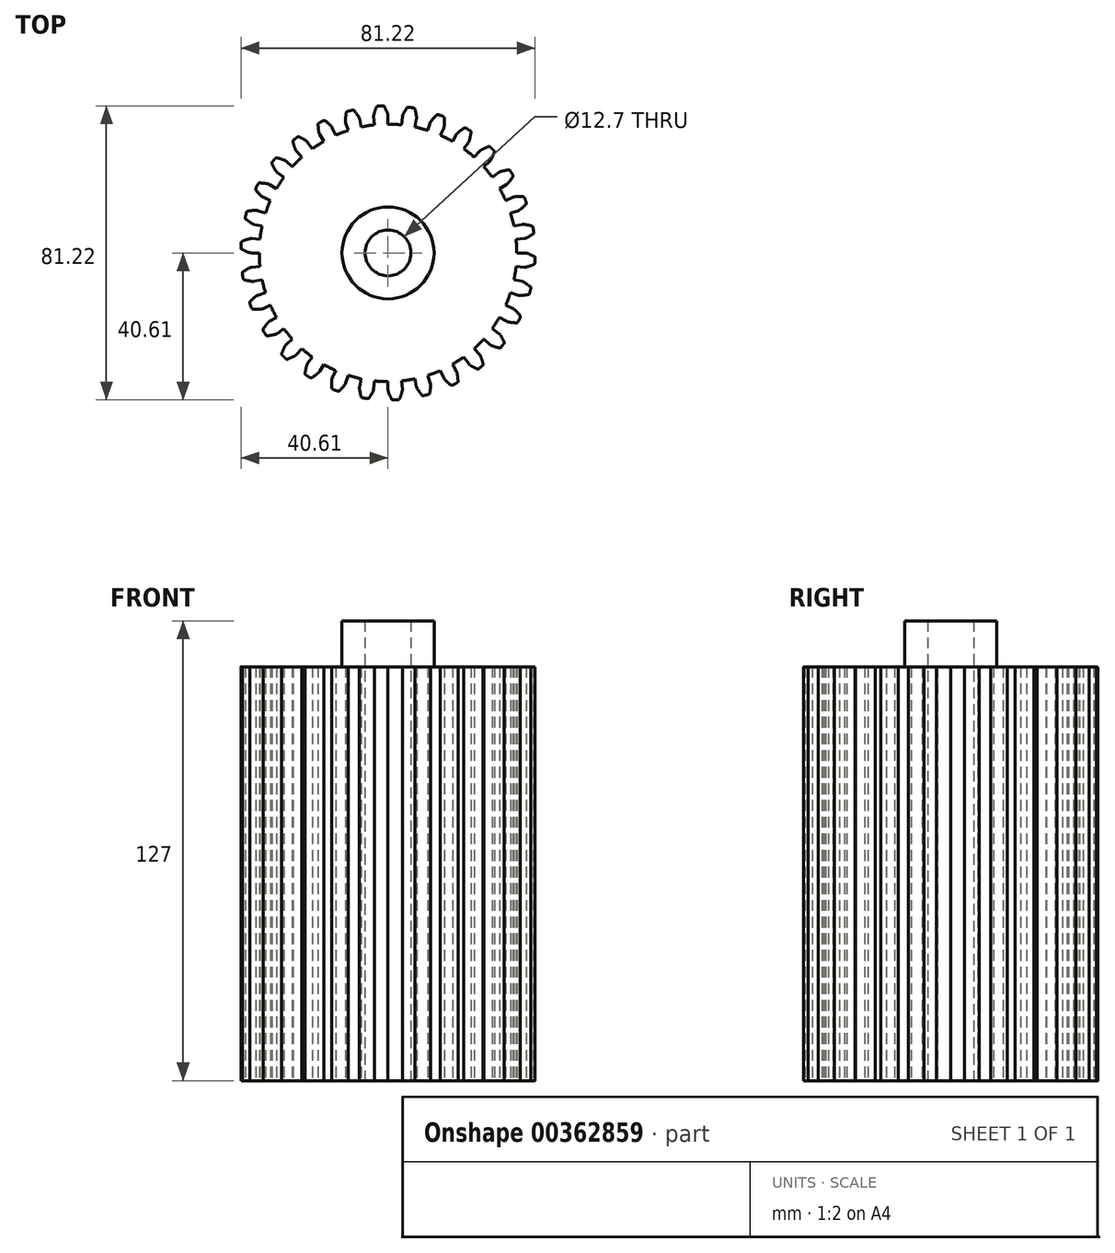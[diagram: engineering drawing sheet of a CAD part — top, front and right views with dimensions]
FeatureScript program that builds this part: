
annotation { "Feature Type Name" : "Feature", "Feature Type Description" : "" }
export const myFeature = defineFeature(function(context is Context, id is Id, definition is map)
    precondition{}
    {
        {
            var Q0;
            Q0=qCreatedBy(makeId("Top.planeOp"),FACE);
            var sketch = newSketch(context, id + "F0", { "sketchPlane" : qUnion([Q0])});
            skArc(sketch, "E0", {"start": v(-1.45, 40.61) * mm, "mid": v(-2.13, 40.58) * mm, "end": v(-2.8, 40.54) * mm});
            skArc(sketch, "E1", {"start": v(-3.72, 35.37) * mm, "mid": v(-5.56, 35.12) * mm, "end": v(-7.4, 34.78) * mm});
            skLineSegment(sketch, "E2", {"start": v(0, 37.81) * mm, "end": v(0, 35.56) * mm});
            skArc(sketch, "E3.trimOffspring", {"start": v(-0.1, 38.38) * mm, "mid": v(-0.51, 39.37) * mm, "end": v(-0.98, 40.34) * mm});
            skArc(sketch, "E4.MirrorCS", {"start": v(-3.9, 38.18) * mm, "mid": v(-3.6, 39.2) * mm, "end": v(-3.25, 40.22) * mm});
            skLineSegment(sketch, "E5.MirrorCS", {"start": v(-3.72, 35.37) * mm, "end": v(-3.95, 37.6) * mm});
            skPoint(sketch, "E6.visualSharp", {"position": v(-1.12, 40.62) * mm});
            skArc(sketch, "E6.filletArc", {"start": v(-0.98, 40.34) * mm, "mid": v(-1.17, 40.54) * mm, "end": v(-1.45, 40.61) * mm});
            skPoint(sketch, "E7.visualSharp", {"position": v(-3.13, 40.52) * mm});
            skArc(sketch, "E7.filletArc", {"start": v(-2.8, 40.54) * mm, "mid": v(-3.07, 40.44) * mm, "end": v(-3.25, 40.22) * mm});
            skPoint(sketch, "E8.visualSharp", {"position": v(0, 38.1) * mm});
            skArc(sketch, "E8.filletArc", {"start": v(0, 37.81) * mm, "mid": v(-0.03, 38.1) * mm, "end": v(-0.1, 38.38) * mm});
            skPoint(sketch, "E9.visualSharp", {"position": v(-3.98, 37.9) * mm});
            skArc(sketch, "E9.filletArc", {"start": v(-3.9, 38.18) * mm, "mid": v(-3.96, 37.9) * mm, "end": v(-3.95, 37.6) * mm});
            skLineSegment(sketch, "E10.1.0", {"start": v(-7.86, 36.99) * mm, "end": v(-7.4, 34.78) * mm});
            skArc(sketch, "E10.1.1", {"start": v(-7.86, 36.99) * mm, "mid": v(-7.95, 37.26) * mm, "end": v(-8.08, 37.52) * mm});
            skArc(sketch, "E10.1.2", {"start": v(-8.08, 37.52) * mm, "mid": v(-8.69, 38.4) * mm, "end": v(-9.34, 39.25) * mm});
            skArc(sketch, "E10.1.3", {"start": v(-9.34, 39.25) * mm, "mid": v(-9.57, 39.42) * mm, "end": v(-9.86, 39.43) * mm});
            skArc(sketch, "E10.1.4", {"start": v(-9.86, 39.43) * mm, "mid": v(-10.52, 39.26) * mm, "end": v(-11.18, 39.07) * mm});
            skArc(sketch, "E10.1.5", {"start": v(-11.18, 39.07) * mm, "mid": v(-11.42, 38.92) * mm, "end": v(-11.54, 38.66) * mm});
            skArc(sketch, "E10.1.6", {"start": v(-11.76, 36.53) * mm, "mid": v(-11.68, 37.6) * mm, "end": v(-11.54, 38.66) * mm});
            skArc(sketch, "E10.1.7", {"start": v(-11.76, 36.53) * mm, "mid": v(-11.75, 36.24) * mm, "end": v(-11.69, 35.96) * mm});
            skLineSegment(sketch, "E10.1.8", {"start": v(-10.99, 33.82) * mm, "end": v(-11.69, 35.96) * mm});
            skLineSegment(sketch, "E10.2.0", {"start": v(-15.38, 34.54) * mm, "end": v(-14.46, 32.49) * mm});
            skArc(sketch, "E10.2.1", {"start": v(-15.38, 34.54) * mm, "mid": v(-15.52, 34.8) * mm, "end": v(-15.7, 35.02) * mm});
            skArc(sketch, "E10.2.2", {"start": v(-15.7, 35.02) * mm, "mid": v(-16.48, 35.76) * mm, "end": v(-17.3, 36.45) * mm});
            skArc(sketch, "E10.2.3", {"start": v(-17.3, 36.45) * mm, "mid": v(-17.56, 36.56) * mm, "end": v(-17.84, 36.52) * mm});
            skArc(sketch, "E10.2.4", {"start": v(-17.84, 36.52) * mm, "mid": v(-18.45, 36.21) * mm, "end": v(-19.06, 35.9) * mm});
            skArc(sketch, "E10.2.5", {"start": v(-19.06, 35.9) * mm, "mid": v(-19.26, 35.7) * mm, "end": v(-19.32, 35.42) * mm});
            skArc(sketch, "E10.2.6", {"start": v(-19.1, 33.29) * mm, "mid": v(-19.24, 34.35) * mm, "end": v(-19.32, 35.42) * mm});
            skArc(sketch, "E10.2.7", {"start": v(-19.1, 33.29) * mm, "mid": v(-19.03, 33) * mm, "end": v(-18.9, 32.75) * mm});
            skLineSegment(sketch, "E10.2.8", {"start": v(-17.78, 30.8) * mm, "end": v(-18.9, 32.75) * mm});
            skLineSegment(sketch, "E10.3.0", {"start": v(-22.23, 30.6) * mm, "end": v(-20.9, 28.77) * mm});
            skArc(sketch, "E10.3.1", {"start": v(-22.23, 30.6) * mm, "mid": v(-22.42, 30.8) * mm, "end": v(-22.64, 30.99) * mm});
            skArc(sketch, "E10.3.2", {"start": v(-22.64, 30.99) * mm, "mid": v(-23.56, 31.55) * mm, "end": v(-24.5, 32.06) * mm});
            skArc(sketch, "E10.3.3", {"start": v(-24.5, 32.06) * mm, "mid": v(-24.78, 32.11) * mm, "end": v(-25.04, 32) * mm});
            skArc(sketch, "E10.3.4", {"start": v(-25.04, 32) * mm, "mid": v(-25.58, 31.58) * mm, "end": v(-26.1, 31.15) * mm});
            skArc(sketch, "E10.3.5", {"start": v(-26.1, 31.15) * mm, "mid": v(-26.26, 30.91) * mm, "end": v(-26.27, 30.63) * mm});
            skArc(sketch, "E10.3.6", {"start": v(-25.6, 28.6) * mm, "mid": v(-25.96, 29.6) * mm, "end": v(-26.27, 30.63) * mm});
            skArc(sketch, "E10.3.7", {"start": v(-25.6, 28.6) * mm, "mid": v(-25.48, 28.33) * mm, "end": v(-25.3, 28.1) * mm});
            skLineSegment(sketch, "E10.3.8", {"start": v(-23.8, 26.43) * mm, "end": v(-25.3, 28.1) * mm});
            skLineSegment(sketch, "E10.4.0", {"start": v(-28.1, 25.3) * mm, "end": v(-26.43, 23.8) * mm});
            skArc(sketch, "E10.4.1", {"start": v(-28.1, 25.3) * mm, "mid": v(-28.33, 25.48) * mm, "end": v(-28.6, 25.6) * mm});
            skArc(sketch, "E10.4.2", {"start": v(-28.6, 25.6) * mm, "mid": v(-29.6, 25.96) * mm, "end": v(-30.63, 26.27) * mm});
            skArc(sketch, "E10.4.3", {"start": v(-30.63, 26.27) * mm, "mid": v(-30.91, 26.26) * mm, "end": v(-31.15, 26.1) * mm});
            skArc(sketch, "E10.4.4", {"start": v(-31.15, 26.1) * mm, "mid": v(-31.58, 25.58) * mm, "end": v(-32, 25.04) * mm});
            skArc(sketch, "E10.4.5", {"start": v(-32, 25.04) * mm, "mid": v(-32.11, 24.78) * mm, "end": v(-32.06, 24.5) * mm});
            skArc(sketch, "E10.4.6", {"start": v(-30.99, 22.64) * mm, "mid": v(-31.55, 23.56) * mm, "end": v(-32.06, 24.5) * mm});
            skArc(sketch, "E10.4.7", {"start": v(-30.99, 22.64) * mm, "mid": v(-30.8, 22.42) * mm, "end": v(-30.6, 22.23) * mm});
            skLineSegment(sketch, "E10.4.8", {"start": v(-28.77, 20.9) * mm, "end": v(-30.6, 22.23) * mm});
            skLineSegment(sketch, "E10.5.0", {"start": v(-32.75, 18.9) * mm, "end": v(-30.8, 17.78) * mm});
            skArc(sketch, "E10.5.1", {"start": v(-32.75, 18.9) * mm, "mid": v(-33, 19.03) * mm, "end": v(-33.29, 19.1) * mm});
            skArc(sketch, "E10.5.2", {"start": v(-33.29, 19.1) * mm, "mid": v(-34.35, 19.24) * mm, "end": v(-35.42, 19.32) * mm});
            skArc(sketch, "E10.5.3", {"start": v(-35.42, 19.32) * mm, "mid": v(-35.7, 19.26) * mm, "end": v(-35.9, 19.06) * mm});
            skArc(sketch, "E10.5.4", {"start": v(-35.9, 19.06) * mm, "mid": v(-36.21, 18.45) * mm, "end": v(-36.52, 17.84) * mm});
            skArc(sketch, "E10.5.5", {"start": v(-36.52, 17.84) * mm, "mid": v(-36.56, 17.56) * mm, "end": v(-36.45, 17.3) * mm});
            skArc(sketch, "E10.5.6", {"start": v(-35.02, 15.7) * mm, "mid": v(-35.76, 16.48) * mm, "end": v(-36.45, 17.3) * mm});
            skArc(sketch, "E10.5.7", {"start": v(-35.02, 15.7) * mm, "mid": v(-34.8, 15.52) * mm, "end": v(-34.54, 15.38) * mm});
            skLineSegment(sketch, "E10.5.8", {"start": v(-32.49, 14.46) * mm, "end": v(-34.54, 15.38) * mm});
            skLineSegment(sketch, "E10.6.0", {"start": v(-35.96, 11.69) * mm, "end": v(-33.82, 10.99) * mm});
            skArc(sketch, "E10.6.1", {"start": v(-35.96, 11.69) * mm, "mid": v(-36.24, 11.75) * mm, "end": v(-36.53, 11.76) * mm});
            skArc(sketch, "E10.6.2", {"start": v(-36.53, 11.76) * mm, "mid": v(-37.6, 11.68) * mm, "end": v(-38.66, 11.54) * mm});
            skArc(sketch, "E10.6.3", {"start": v(-38.66, 11.54) * mm, "mid": v(-38.92, 11.42) * mm, "end": v(-39.07, 11.18) * mm});
            skArc(sketch, "E10.6.4", {"start": v(-39.07, 11.18) * mm, "mid": v(-39.26, 10.52) * mm, "end": v(-39.43, 9.86) * mm});
            skArc(sketch, "E10.6.5", {"start": v(-39.43, 9.86) * mm, "mid": v(-39.42, 9.57) * mm, "end": v(-39.25, 9.34) * mm});
            skArc(sketch, "E10.6.6", {"start": v(-37.52, 8.08) * mm, "mid": v(-38.4, 8.69) * mm, "end": v(-39.25, 9.34) * mm});
            skArc(sketch, "E10.6.7", {"start": v(-37.52, 8.08) * mm, "mid": v(-37.26, 7.95) * mm, "end": v(-36.99, 7.86) * mm});
            skLineSegment(sketch, "E10.6.8", {"start": v(-34.78, 7.4) * mm, "end": v(-36.99, 7.86) * mm});
            skLineSegment(sketch, "E10.7.0", {"start": v(-37.6, 3.95) * mm, "end": v(-35.37, 3.72) * mm});
            skArc(sketch, "E10.7.1", {"start": v(-37.6, 3.95) * mm, "mid": v(-37.9, 3.96) * mm, "end": v(-38.18, 3.9) * mm});
            skArc(sketch, "E10.7.2", {"start": v(-38.18, 3.9) * mm, "mid": v(-39.2, 3.6) * mm, "end": v(-40.22, 3.25) * mm});
            skArc(sketch, "E10.7.3", {"start": v(-40.22, 3.25) * mm, "mid": v(-40.44, 3.07) * mm, "end": v(-40.54, 2.8) * mm});
            skArc(sketch, "E10.7.4", {"start": v(-40.54, 2.8) * mm, "mid": v(-40.58, 2.13) * mm, "end": v(-40.61, 1.45) * mm});
            skArc(sketch, "E10.7.5", {"start": v(-40.61, 1.45) * mm, "mid": v(-40.54, 1.17) * mm, "end": v(-40.34, 0.98) * mm});
            skArc(sketch, "E10.7.6", {"start": v(-38.38, 0.1) * mm, "mid": v(-39.37, 0.51) * mm, "end": v(-40.34, 0.98) * mm});
            skArc(sketch, "E10.7.7", {"start": v(-38.38, 0.1) * mm, "mid": v(-38.1, 0.03) * mm, "end": v(-37.81, 0) * mm});
            skLineSegment(sketch, "E10.7.8", {"start": v(-35.56, 0) * mm, "end": v(-37.81, 0) * mm});
            skLineSegment(sketch, "E10.8.0", {"start": v(-37.6, -3.95) * mm, "end": v(-35.37, -3.72) * mm});
            skArc(sketch, "E10.8.1", {"start": v(-37.6, -3.95) * mm, "mid": v(-37.9, -4) * mm, "end": v(-38.16, -4.12) * mm});
            skArc(sketch, "E10.8.2", {"start": v(-38.16, -4.12) * mm, "mid": v(-39.1, -4.63) * mm, "end": v(-40.02, -5.19) * mm});
            skArc(sketch, "E10.8.3", {"start": v(-40.02, -5.19) * mm, "mid": v(-40.2, -5.4) * mm, "end": v(-40.24, -5.68) * mm});
            skArc(sketch, "E10.8.4", {"start": v(-40.24, -5.68) * mm, "mid": v(-40.14, -6.36) * mm, "end": v(-40.03, -7.03) * mm});
            skArc(sketch, "E10.8.5", {"start": v(-40.03, -7.03) * mm, "mid": v(-39.9, -7.29) * mm, "end": v(-39.66, -7.43) * mm});
            skArc(sketch, "E10.8.6", {"start": v(-37.56, -7.88) * mm, "mid": v(-38.62, -7.68) * mm, "end": v(-39.66, -7.43) * mm});
            skArc(sketch, "E10.8.7", {"start": v(-37.56, -7.88) * mm, "mid": v(-37.27, -7.9) * mm, "end": v(-36.99, -7.86) * mm});
            skLineSegment(sketch, "E10.8.8", {"start": v(-34.78, -7.4) * mm, "end": v(-36.99, -7.86) * mm});
            skLineSegment(sketch, "E10.9.0", {"start": v(-35.96, -11.69) * mm, "end": v(-33.82, -10.99) * mm});
            skArc(sketch, "E10.9.1", {"start": v(-35.96, -11.69) * mm, "mid": v(-36.23, -11.8) * mm, "end": v(-36.47, -11.96) * mm});
            skArc(sketch, "E10.9.2", {"start": v(-36.47, -11.96) * mm, "mid": v(-37.29, -12.65) * mm, "end": v(-38.06, -13.4) * mm});
            skArc(sketch, "E10.9.3", {"start": v(-38.06, -13.4) * mm, "mid": v(-38.2, -13.64) * mm, "end": v(-38.18, -13.93) * mm});
            skArc(sketch, "E10.9.4", {"start": v(-38.18, -13.93) * mm, "mid": v(-37.94, -14.56) * mm, "end": v(-37.7, -15.2) * mm});
            skArc(sketch, "E10.9.5", {"start": v(-37.7, -15.2) * mm, "mid": v(-37.52, -15.42) * mm, "end": v(-37.25, -15.52) * mm});
            skArc(sketch, "E10.9.6", {"start": v(-35.1, -15.52) * mm, "mid": v(-36.18, -15.54) * mm, "end": v(-37.25, -15.52) * mm});
            skArc(sketch, "E10.9.7", {"start": v(-35.1, -15.52) * mm, "mid": v(-34.82, -15.47) * mm, "end": v(-34.54, -15.38) * mm});
            skLineSegment(sketch, "E10.9.8", {"start": v(-32.49, -14.46) * mm, "end": v(-34.54, -15.38) * mm});
            skLineSegment(sketch, "E10.10.0", {"start": v(-32.75, -18.9) * mm, "end": v(-30.8, -17.78) * mm});
            skArc(sketch, "E10.10.1", {"start": v(-32.75, -18.9) * mm, "mid": v(-32.98, -19.07) * mm, "end": v(-33.19, -19.28) * mm});
            skArc(sketch, "E10.10.2", {"start": v(-33.19, -19.28) * mm, "mid": v(-33.84, -20.13) * mm, "end": v(-34.45, -21.01) * mm});
            skArc(sketch, "E10.10.3", {"start": v(-34.45, -21.01) * mm, "mid": v(-34.53, -21.29) * mm, "end": v(-34.45, -21.56) * mm});
            skArc(sketch, "E10.10.4", {"start": v(-34.45, -21.56) * mm, "mid": v(-34.08, -22.13) * mm, "end": v(-33.7, -22.7) * mm});
            skArc(sketch, "E10.10.5", {"start": v(-33.7, -22.7) * mm, "mid": v(-33.49, -22.88) * mm, "end": v(-33.2, -22.92) * mm});
            skArc(sketch, "E10.10.6", {"start": v(-31.11, -22.47) * mm, "mid": v(-32.15, -22.73) * mm, "end": v(-33.2, -22.92) * mm});
            skArc(sketch, "E10.10.7", {"start": v(-31.11, -22.47) * mm, "mid": v(-30.84, -22.37) * mm, "end": v(-30.6, -22.23) * mm});
            skLineSegment(sketch, "E10.10.8", {"start": v(-28.77, -20.9) * mm, "end": v(-30.6, -22.23) * mm});
            skLineSegment(sketch, "E10.11.0", {"start": v(-28.1, -25.3) * mm, "end": v(-26.43, -23.8) * mm});
            skArc(sketch, "E10.11.1", {"start": v(-28.1, -25.3) * mm, "mid": v(-28.3, -25.51) * mm, "end": v(-28.45, -25.76) * mm});
            skArc(sketch, "E10.11.2", {"start": v(-28.45, -25.76) * mm, "mid": v(-28.91, -26.73) * mm, "end": v(-29.32, -27.72) * mm});
            skArc(sketch, "E10.11.3", {"start": v(-29.32, -27.72) * mm, "mid": v(-29.35, -28) * mm, "end": v(-29.22, -28.25) * mm});
            skArc(sketch, "E10.11.4", {"start": v(-29.22, -28.25) * mm, "mid": v(-28.74, -28.74) * mm, "end": v(-28.25, -29.22) * mm});
            skArc(sketch, "E10.11.5", {"start": v(-28.25, -29.22) * mm, "mid": v(-28, -29.35) * mm, "end": v(-27.72, -29.32) * mm});
            skArc(sketch, "E10.11.6", {"start": v(-25.76, -28.45) * mm, "mid": v(-26.73, -28.91) * mm, "end": v(-27.72, -29.32) * mm});
            skArc(sketch, "E10.11.7", {"start": v(-25.76, -28.45) * mm, "mid": v(-25.51, -28.3) * mm, "end": v(-25.3, -28.1) * mm});
            skLineSegment(sketch, "E10.11.8", {"start": v(-23.8, -26.43) * mm, "end": v(-25.3, -28.1) * mm});
            skLineSegment(sketch, "E10.12.0", {"start": v(-22.23, -30.6) * mm, "end": v(-20.9, -28.77) * mm});
            skArc(sketch, "E10.12.1", {"start": v(-22.23, -30.6) * mm, "mid": v(-22.37, -30.84) * mm, "end": v(-22.47, -31.11) * mm});
            skArc(sketch, "E10.12.2", {"start": v(-22.47, -31.11) * mm, "mid": v(-22.73, -32.15) * mm, "end": v(-22.92, -33.2) * mm});
            skArc(sketch, "E10.12.3", {"start": v(-22.92, -33.2) * mm, "mid": v(-22.88, -33.49) * mm, "end": v(-22.7, -33.7) * mm});
            skArc(sketch, "E10.12.4", {"start": v(-22.7, -33.7) * mm, "mid": v(-22.13, -34.08) * mm, "end": v(-21.56, -34.45) * mm});
            skArc(sketch, "E10.12.5", {"start": v(-21.56, -34.45) * mm, "mid": v(-21.29, -34.53) * mm, "end": v(-21.01, -34.45) * mm});
            skArc(sketch, "E10.12.6", {"start": v(-19.28, -33.19) * mm, "mid": v(-20.13, -33.84) * mm, "end": v(-21.01, -34.45) * mm});
            skArc(sketch, "E10.12.7", {"start": v(-19.28, -33.19) * mm, "mid": v(-19.07, -32.98) * mm, "end": v(-18.9, -32.75) * mm});
            skLineSegment(sketch, "E10.12.8", {"start": v(-17.78, -30.8) * mm, "end": v(-18.9, -32.75) * mm});
            skLineSegment(sketch, "E10.13.0", {"start": v(-15.38, -34.54) * mm, "end": v(-14.46, -32.49) * mm});
            skArc(sketch, "E10.13.1", {"start": v(-15.38, -34.54) * mm, "mid": v(-15.47, -34.82) * mm, "end": v(-15.52, -35.1) * mm});
            skArc(sketch, "E10.13.2", {"start": v(-15.52, -35.1) * mm, "mid": v(-15.54, -36.18) * mm, "end": v(-15.52, -37.25) * mm});
            skArc(sketch, "E10.13.3", {"start": v(-15.52, -37.25) * mm, "mid": v(-15.42, -37.52) * mm, "end": v(-15.2, -37.7) * mm});
            skArc(sketch, "E10.13.4", {"start": v(-15.2, -37.7) * mm, "mid": v(-14.56, -37.94) * mm, "end": v(-13.93, -38.18) * mm});
            skArc(sketch, "E10.13.5", {"start": v(-13.93, -38.18) * mm, "mid": v(-13.64, -38.2) * mm, "end": v(-13.4, -38.06) * mm});
            skArc(sketch, "E10.13.6", {"start": v(-11.96, -36.47) * mm, "mid": v(-12.65, -37.29) * mm, "end": v(-13.4, -38.06) * mm});
            skArc(sketch, "E10.13.7", {"start": v(-11.96, -36.47) * mm, "mid": v(-11.8, -36.23) * mm, "end": v(-11.69, -35.96) * mm});
            skLineSegment(sketch, "E10.13.8", {"start": v(-10.99, -33.82) * mm, "end": v(-11.69, -35.96) * mm});
            skLineSegment(sketch, "E10.14.0", {"start": v(-7.86, -36.99) * mm, "end": v(-7.4, -34.78) * mm});
            skArc(sketch, "E10.14.1", {"start": v(-7.86, -36.99) * mm, "mid": v(-7.9, -37.27) * mm, "end": v(-7.88, -37.56) * mm});
            skArc(sketch, "E10.14.2", {"start": v(-7.88, -37.56) * mm, "mid": v(-7.68, -38.62) * mm, "end": v(-7.43, -39.66) * mm});
            skArc(sketch, "E10.14.3", {"start": v(-7.43, -39.66) * mm, "mid": v(-7.29, -39.9) * mm, "end": v(-7.03, -40.03) * mm});
            skArc(sketch, "E10.14.4", {"start": v(-7.03, -40.03) * mm, "mid": v(-6.36, -40.14) * mm, "end": v(-5.68, -40.24) * mm});
            skArc(sketch, "E10.14.5", {"start": v(-5.68, -40.24) * mm, "mid": v(-5.4, -40.2) * mm, "end": v(-5.19, -40.02) * mm});
            skArc(sketch, "E10.14.6", {"start": v(-4.12, -38.16) * mm, "mid": v(-4.63, -39.1) * mm, "end": v(-5.19, -40.02) * mm});
            skArc(sketch, "E10.14.7", {"start": v(-4.12, -38.16) * mm, "mid": v(-4, -37.9) * mm, "end": v(-3.95, -37.6) * mm});
            skLineSegment(sketch, "E10.14.8", {"start": v(-3.72, -35.37) * mm, "end": v(-3.95, -37.6) * mm});
            skLineSegment(sketch, "E10.15.0", {"start": v(0, -37.81) * mm, "end": v(0, -35.56) * mm});
            skArc(sketch, "E10.15.1", {"start": v(0, -37.81) * mm, "mid": v(0.03, -38.1) * mm, "end": v(0.1, -38.38) * mm});
            skArc(sketch, "E10.15.2", {"start": v(0.1, -38.38) * mm, "mid": v(0.51, -39.37) * mm, "end": v(0.98, -40.34) * mm});
            skArc(sketch, "E10.15.3", {"start": v(0.98, -40.34) * mm, "mid": v(1.17, -40.54) * mm, "end": v(1.45, -40.61) * mm});
            skArc(sketch, "E10.15.4", {"start": v(1.45, -40.61) * mm, "mid": v(2.13, -40.58) * mm, "end": v(2.8, -40.54) * mm});
            skArc(sketch, "E10.15.5", {"start": v(2.8, -40.54) * mm, "mid": v(3.07, -40.44) * mm, "end": v(3.25, -40.22) * mm});
            skArc(sketch, "E10.15.6", {"start": v(3.9, -38.18) * mm, "mid": v(3.6, -39.2) * mm, "end": v(3.25, -40.22) * mm});
            skArc(sketch, "E10.15.7", {"start": v(3.9, -38.18) * mm, "mid": v(3.96, -37.9) * mm, "end": v(3.95, -37.6) * mm});
            skLineSegment(sketch, "E10.15.8", {"start": v(3.72, -35.37) * mm, "end": v(3.95, -37.6) * mm});
            skLineSegment(sketch, "E10.16.0", {"start": v(7.86, -36.99) * mm, "end": v(7.4, -34.78) * mm});
            skArc(sketch, "E10.16.1", {"start": v(7.86, -36.99) * mm, "mid": v(7.95, -37.26) * mm, "end": v(8.08, -37.52) * mm});
            skArc(sketch, "E10.16.2", {"start": v(8.08, -37.52) * mm, "mid": v(8.69, -38.4) * mm, "end": v(9.34, -39.25) * mm});
            skArc(sketch, "E10.16.3", {"start": v(9.34, -39.25) * mm, "mid": v(9.57, -39.42) * mm, "end": v(9.86, -39.43) * mm});
            skArc(sketch, "E10.16.4", {"start": v(9.86, -39.43) * mm, "mid": v(10.52, -39.26) * mm, "end": v(11.18, -39.07) * mm});
            skArc(sketch, "E10.16.5", {"start": v(11.18, -39.07) * mm, "mid": v(11.42, -38.92) * mm, "end": v(11.54, -38.66) * mm});
            skArc(sketch, "E10.16.6", {"start": v(11.76, -36.53) * mm, "mid": v(11.68, -37.6) * mm, "end": v(11.54, -38.66) * mm});
            skArc(sketch, "E10.16.7", {"start": v(11.76, -36.53) * mm, "mid": v(11.75, -36.24) * mm, "end": v(11.69, -35.96) * mm});
            skLineSegment(sketch, "E10.16.8", {"start": v(10.99, -33.82) * mm, "end": v(11.69, -35.96) * mm});
            skLineSegment(sketch, "E10.17.0", {"start": v(15.38, -34.54) * mm, "end": v(14.46, -32.49) * mm});
            skArc(sketch, "E10.17.1", {"start": v(15.38, -34.54) * mm, "mid": v(15.52, -34.8) * mm, "end": v(15.7, -35.02) * mm});
            skArc(sketch, "E10.17.2", {"start": v(15.7, -35.02) * mm, "mid": v(16.48, -35.76) * mm, "end": v(17.3, -36.45) * mm});
            skArc(sketch, "E10.17.3", {"start": v(17.3, -36.45) * mm, "mid": v(17.56, -36.56) * mm, "end": v(17.84, -36.52) * mm});
            skArc(sketch, "E10.17.4", {"start": v(17.84, -36.52) * mm, "mid": v(18.45, -36.21) * mm, "end": v(19.06, -35.9) * mm});
            skArc(sketch, "E10.17.5", {"start": v(19.06, -35.9) * mm, "mid": v(19.26, -35.7) * mm, "end": v(19.32, -35.42) * mm});
            skArc(sketch, "E10.17.6", {"start": v(19.1, -33.29) * mm, "mid": v(19.24, -34.35) * mm, "end": v(19.32, -35.42) * mm});
            skArc(sketch, "E10.17.7", {"start": v(19.1, -33.29) * mm, "mid": v(19.03, -33) * mm, "end": v(18.9, -32.75) * mm});
            skLineSegment(sketch, "E10.17.8", {"start": v(17.78, -30.8) * mm, "end": v(18.9, -32.75) * mm});
            skLineSegment(sketch, "E10.18.0", {"start": v(22.23, -30.6) * mm, "end": v(20.9, -28.77) * mm});
            skArc(sketch, "E10.18.1", {"start": v(22.23, -30.6) * mm, "mid": v(22.42, -30.8) * mm, "end": v(22.64, -30.99) * mm});
            skArc(sketch, "E10.18.2", {"start": v(22.64, -30.99) * mm, "mid": v(23.56, -31.55) * mm, "end": v(24.5, -32.06) * mm});
            skArc(sketch, "E10.18.3", {"start": v(24.5, -32.06) * mm, "mid": v(24.78, -32.11) * mm, "end": v(25.04, -32) * mm});
            skArc(sketch, "E10.18.4", {"start": v(25.04, -32) * mm, "mid": v(25.58, -31.58) * mm, "end": v(26.1, -31.15) * mm});
            skArc(sketch, "E10.18.5", {"start": v(26.1, -31.15) * mm, "mid": v(26.26, -30.91) * mm, "end": v(26.27, -30.63) * mm});
            skArc(sketch, "E10.18.6", {"start": v(25.6, -28.6) * mm, "mid": v(25.96, -29.6) * mm, "end": v(26.27, -30.63) * mm});
            skArc(sketch, "E10.18.7", {"start": v(25.6, -28.6) * mm, "mid": v(25.48, -28.33) * mm, "end": v(25.3, -28.1) * mm});
            skLineSegment(sketch, "E10.18.8", {"start": v(23.8, -26.43) * mm, "end": v(25.3, -28.1) * mm});
            skLineSegment(sketch, "E10.19.0", {"start": v(28.1, -25.3) * mm, "end": v(26.43, -23.8) * mm});
            skArc(sketch, "E10.19.1", {"start": v(28.1, -25.3) * mm, "mid": v(28.33, -25.48) * mm, "end": v(28.6, -25.6) * mm});
            skArc(sketch, "E10.19.2", {"start": v(28.6, -25.6) * mm, "mid": v(29.6, -25.96) * mm, "end": v(30.63, -26.27) * mm});
            skArc(sketch, "E10.19.3", {"start": v(30.63, -26.27) * mm, "mid": v(30.91, -26.26) * mm, "end": v(31.15, -26.1) * mm});
            skArc(sketch, "E10.19.4", {"start": v(31.15, -26.1) * mm, "mid": v(31.58, -25.58) * mm, "end": v(32, -25.04) * mm});
            skArc(sketch, "E10.19.5", {"start": v(32, -25.04) * mm, "mid": v(32.11, -24.78) * mm, "end": v(32.06, -24.5) * mm});
            skArc(sketch, "E10.19.6", {"start": v(30.99, -22.64) * mm, "mid": v(31.55, -23.56) * mm, "end": v(32.06, -24.5) * mm});
            skArc(sketch, "E10.19.7", {"start": v(30.99, -22.64) * mm, "mid": v(30.8, -22.42) * mm, "end": v(30.6, -22.23) * mm});
            skLineSegment(sketch, "E10.19.8", {"start": v(28.77, -20.9) * mm, "end": v(30.6, -22.23) * mm});
            skLineSegment(sketch, "E10.20.0", {"start": v(32.75, -18.9) * mm, "end": v(30.8, -17.78) * mm});
            skArc(sketch, "E10.20.1", {"start": v(32.75, -18.9) * mm, "mid": v(33, -19.03) * mm, "end": v(33.29, -19.1) * mm});
            skArc(sketch, "E10.20.2", {"start": v(33.29, -19.1) * mm, "mid": v(34.35, -19.24) * mm, "end": v(35.42, -19.32) * mm});
            skArc(sketch, "E10.20.3", {"start": v(35.42, -19.32) * mm, "mid": v(35.7, -19.26) * mm, "end": v(35.9, -19.06) * mm});
            skArc(sketch, "E10.20.4", {"start": v(35.9, -19.06) * mm, "mid": v(36.21, -18.45) * mm, "end": v(36.52, -17.84) * mm});
            skArc(sketch, "E10.20.5", {"start": v(36.52, -17.84) * mm, "mid": v(36.56, -17.56) * mm, "end": v(36.45, -17.3) * mm});
            skArc(sketch, "E10.20.6", {"start": v(35.02, -15.7) * mm, "mid": v(35.76, -16.48) * mm, "end": v(36.45, -17.3) * mm});
            skArc(sketch, "E10.20.7", {"start": v(35.02, -15.7) * mm, "mid": v(34.8, -15.52) * mm, "end": v(34.54, -15.38) * mm});
            skLineSegment(sketch, "E10.20.8", {"start": v(32.49, -14.46) * mm, "end": v(34.54, -15.38) * mm});
            skLineSegment(sketch, "E10.21.0", {"start": v(35.96, -11.69) * mm, "end": v(33.82, -10.99) * mm});
            skArc(sketch, "E10.21.1", {"start": v(35.96, -11.69) * mm, "mid": v(36.24, -11.75) * mm, "end": v(36.53, -11.76) * mm});
            skArc(sketch, "E10.21.2", {"start": v(36.53, -11.76) * mm, "mid": v(37.6, -11.68) * mm, "end": v(38.66, -11.54) * mm});
            skArc(sketch, "E10.21.3", {"start": v(38.66, -11.54) * mm, "mid": v(38.92, -11.42) * mm, "end": v(39.07, -11.18) * mm});
            skArc(sketch, "E10.21.4", {"start": v(39.07, -11.18) * mm, "mid": v(39.26, -10.52) * mm, "end": v(39.43, -9.86) * mm});
            skArc(sketch, "E10.21.5", {"start": v(39.43, -9.86) * mm, "mid": v(39.42, -9.57) * mm, "end": v(39.25, -9.34) * mm});
            skArc(sketch, "E10.21.6", {"start": v(37.52, -8.08) * mm, "mid": v(38.4, -8.69) * mm, "end": v(39.25, -9.34) * mm});
            skArc(sketch, "E10.21.7", {"start": v(37.52, -8.08) * mm, "mid": v(37.26, -7.95) * mm, "end": v(36.99, -7.86) * mm});
            skLineSegment(sketch, "E10.21.8", {"start": v(34.78, -7.4) * mm, "end": v(36.99, -7.86) * mm});
            skLineSegment(sketch, "E10.22.0", {"start": v(37.6, -3.95) * mm, "end": v(35.37, -3.72) * mm});
            skArc(sketch, "E10.22.1", {"start": v(37.6, -3.95) * mm, "mid": v(37.9, -3.96) * mm, "end": v(38.18, -3.9) * mm});
            skArc(sketch, "E10.22.2", {"start": v(38.18, -3.9) * mm, "mid": v(39.2, -3.6) * mm, "end": v(40.22, -3.25) * mm});
            skArc(sketch, "E10.22.3", {"start": v(40.22, -3.25) * mm, "mid": v(40.44, -3.07) * mm, "end": v(40.54, -2.8) * mm});
            skArc(sketch, "E10.22.4", {"start": v(40.54, -2.8) * mm, "mid": v(40.58, -2.13) * mm, "end": v(40.61, -1.45) * mm});
            skArc(sketch, "E10.22.5", {"start": v(40.61, -1.45) * mm, "mid": v(40.54, -1.17) * mm, "end": v(40.34, -0.98) * mm});
            skArc(sketch, "E10.22.6", {"start": v(38.38, -0.1) * mm, "mid": v(39.37, -0.51) * mm, "end": v(40.34, -0.98) * mm});
            skArc(sketch, "E10.22.7", {"start": v(38.38, -0.1) * mm, "mid": v(38.1, -0.03) * mm, "end": v(37.81, 0) * mm});
            skLineSegment(sketch, "E10.22.8", {"start": v(35.56, 0) * mm, "end": v(37.81, 0) * mm});
            skLineSegment(sketch, "E10.23.0", {"start": v(37.6, 3.95) * mm, "end": v(35.37, 3.72) * mm});
            skArc(sketch, "E10.23.1", {"start": v(37.6, 3.95) * mm, "mid": v(37.9, 4) * mm, "end": v(38.16, 4.12) * mm});
            skArc(sketch, "E10.23.2", {"start": v(38.16, 4.12) * mm, "mid": v(39.1, 4.63) * mm, "end": v(40.02, 5.19) * mm});
            skArc(sketch, "E10.23.3", {"start": v(40.02, 5.19) * mm, "mid": v(40.2, 5.4) * mm, "end": v(40.24, 5.68) * mm});
            skArc(sketch, "E10.23.4", {"start": v(40.24, 5.68) * mm, "mid": v(40.14, 6.36) * mm, "end": v(40.03, 7.03) * mm});
            skArc(sketch, "E10.23.5", {"start": v(40.03, 7.03) * mm, "mid": v(39.9, 7.29) * mm, "end": v(39.66, 7.43) * mm});
            skArc(sketch, "E10.23.6", {"start": v(37.56, 7.88) * mm, "mid": v(38.62, 7.68) * mm, "end": v(39.66, 7.43) * mm});
            skArc(sketch, "E10.23.7", {"start": v(37.56, 7.88) * mm, "mid": v(37.27, 7.9) * mm, "end": v(36.99, 7.86) * mm});
            skLineSegment(sketch, "E10.23.8", {"start": v(34.78, 7.4) * mm, "end": v(36.99, 7.86) * mm});
            skLineSegment(sketch, "E10.24.0", {"start": v(35.96, 11.69) * mm, "end": v(33.82, 10.99) * mm});
            skArc(sketch, "E10.24.1", {"start": v(35.96, 11.69) * mm, "mid": v(36.23, 11.8) * mm, "end": v(36.47, 11.96) * mm});
            skArc(sketch, "E10.24.2", {"start": v(36.47, 11.96) * mm, "mid": v(37.29, 12.65) * mm, "end": v(38.06, 13.4) * mm});
            skArc(sketch, "E10.24.3", {"start": v(38.06, 13.4) * mm, "mid": v(38.2, 13.64) * mm, "end": v(38.18, 13.93) * mm});
            skArc(sketch, "E10.24.4", {"start": v(38.18, 13.93) * mm, "mid": v(37.94, 14.56) * mm, "end": v(37.7, 15.2) * mm});
            skArc(sketch, "E10.24.5", {"start": v(37.7, 15.2) * mm, "mid": v(37.52, 15.42) * mm, "end": v(37.25, 15.52) * mm});
            skArc(sketch, "E10.24.6", {"start": v(35.1, 15.52) * mm, "mid": v(36.18, 15.54) * mm, "end": v(37.25, 15.52) * mm});
            skArc(sketch, "E10.24.7", {"start": v(35.1, 15.52) * mm, "mid": v(34.82, 15.47) * mm, "end": v(34.54, 15.38) * mm});
            skLineSegment(sketch, "E10.24.8", {"start": v(32.49, 14.46) * mm, "end": v(34.54, 15.38) * mm});
            skLineSegment(sketch, "E10.25.0", {"start": v(32.75, 18.9) * mm, "end": v(30.8, 17.78) * mm});
            skArc(sketch, "E10.25.1", {"start": v(32.75, 18.9) * mm, "mid": v(32.98, 19.07) * mm, "end": v(33.19, 19.28) * mm});
            skArc(sketch, "E10.25.2", {"start": v(33.19, 19.28) * mm, "mid": v(33.84, 20.13) * mm, "end": v(34.45, 21.01) * mm});
            skArc(sketch, "E10.25.3", {"start": v(34.45, 21.01) * mm, "mid": v(34.53, 21.29) * mm, "end": v(34.45, 21.56) * mm});
            skArc(sketch, "E10.25.4", {"start": v(34.45, 21.56) * mm, "mid": v(34.08, 22.13) * mm, "end": v(33.7, 22.7) * mm});
            skArc(sketch, "E10.25.5", {"start": v(33.7, 22.7) * mm, "mid": v(33.49, 22.88) * mm, "end": v(33.2, 22.92) * mm});
            skArc(sketch, "E10.25.6", {"start": v(31.11, 22.47) * mm, "mid": v(32.15, 22.73) * mm, "end": v(33.2, 22.92) * mm});
            skArc(sketch, "E10.25.7", {"start": v(31.11, 22.47) * mm, "mid": v(30.84, 22.37) * mm, "end": v(30.6, 22.23) * mm});
            skLineSegment(sketch, "E10.25.8", {"start": v(28.77, 20.9) * mm, "end": v(30.6, 22.23) * mm});
            skLineSegment(sketch, "E10.26.0", {"start": v(28.1, 25.3) * mm, "end": v(26.43, 23.8) * mm});
            skArc(sketch, "E10.26.1", {"start": v(28.1, 25.3) * mm, "mid": v(28.3, 25.51) * mm, "end": v(28.45, 25.76) * mm});
            skArc(sketch, "E10.26.2", {"start": v(28.45, 25.76) * mm, "mid": v(28.91, 26.73) * mm, "end": v(29.32, 27.72) * mm});
            skArc(sketch, "E10.26.3", {"start": v(29.32, 27.72) * mm, "mid": v(29.35, 28) * mm, "end": v(29.22, 28.25) * mm});
            skArc(sketch, "E10.26.4", {"start": v(29.22, 28.25) * mm, "mid": v(28.74, 28.74) * mm, "end": v(28.25, 29.22) * mm});
            skArc(sketch, "E10.26.5", {"start": v(28.25, 29.22) * mm, "mid": v(28, 29.35) * mm, "end": v(27.72, 29.32) * mm});
            skArc(sketch, "E10.26.6", {"start": v(25.76, 28.45) * mm, "mid": v(26.73, 28.91) * mm, "end": v(27.72, 29.32) * mm});
            skArc(sketch, "E10.26.7", {"start": v(25.76, 28.45) * mm, "mid": v(25.51, 28.3) * mm, "end": v(25.3, 28.1) * mm});
            skLineSegment(sketch, "E10.26.8", {"start": v(23.8, 26.43) * mm, "end": v(25.3, 28.1) * mm});
            skLineSegment(sketch, "E10.27.0", {"start": v(22.23, 30.6) * mm, "end": v(20.9, 28.77) * mm});
            skArc(sketch, "E10.27.1", {"start": v(22.23, 30.6) * mm, "mid": v(22.37, 30.84) * mm, "end": v(22.47, 31.11) * mm});
            skArc(sketch, "E10.27.2", {"start": v(22.47, 31.11) * mm, "mid": v(22.73, 32.15) * mm, "end": v(22.92, 33.2) * mm});
            skArc(sketch, "E10.27.3", {"start": v(22.92, 33.2) * mm, "mid": v(22.88, 33.49) * mm, "end": v(22.7, 33.7) * mm});
            skArc(sketch, "E10.27.4", {"start": v(22.7, 33.7) * mm, "mid": v(22.13, 34.08) * mm, "end": v(21.56, 34.45) * mm});
            skArc(sketch, "E10.27.5", {"start": v(21.56, 34.45) * mm, "mid": v(21.29, 34.53) * mm, "end": v(21.01, 34.45) * mm});
            skArc(sketch, "E10.27.6", {"start": v(19.28, 33.19) * mm, "mid": v(20.13, 33.84) * mm, "end": v(21.01, 34.45) * mm});
            skArc(sketch, "E10.27.7", {"start": v(19.28, 33.19) * mm, "mid": v(19.07, 32.98) * mm, "end": v(18.9, 32.75) * mm});
            skLineSegment(sketch, "E10.27.8", {"start": v(17.78, 30.8) * mm, "end": v(18.9, 32.75) * mm});
            skLineSegment(sketch, "E10.28.0", {"start": v(15.38, 34.54) * mm, "end": v(14.46, 32.49) * mm});
            skArc(sketch, "E10.28.1", {"start": v(15.38, 34.54) * mm, "mid": v(15.47, 34.82) * mm, "end": v(15.52, 35.1) * mm});
            skArc(sketch, "E10.28.2", {"start": v(15.52, 35.1) * mm, "mid": v(15.54, 36.18) * mm, "end": v(15.52, 37.25) * mm});
            skArc(sketch, "E10.28.3", {"start": v(15.52, 37.25) * mm, "mid": v(15.42, 37.52) * mm, "end": v(15.2, 37.7) * mm});
            skArc(sketch, "E10.28.4", {"start": v(15.2, 37.7) * mm, "mid": v(14.56, 37.94) * mm, "end": v(13.93, 38.18) * mm});
            skArc(sketch, "E10.28.5", {"start": v(13.93, 38.18) * mm, "mid": v(13.64, 38.2) * mm, "end": v(13.4, 38.06) * mm});
            skArc(sketch, "E10.28.6", {"start": v(11.96, 36.47) * mm, "mid": v(12.65, 37.29) * mm, "end": v(13.4, 38.06) * mm});
            skArc(sketch, "E10.28.7", {"start": v(11.96, 36.47) * mm, "mid": v(11.8, 36.23) * mm, "end": v(11.69, 35.96) * mm});
            skLineSegment(sketch, "E10.28.8", {"start": v(10.99, 33.82) * mm, "end": v(11.69, 35.96) * mm});
            skLineSegment(sketch, "E10.29.0", {"start": v(7.86, 36.99) * mm, "end": v(7.4, 34.78) * mm});
            skArc(sketch, "E10.29.1", {"start": v(7.86, 36.99) * mm, "mid": v(7.9, 37.27) * mm, "end": v(7.88, 37.56) * mm});
            skArc(sketch, "E10.29.2", {"start": v(7.88, 37.56) * mm, "mid": v(7.68, 38.62) * mm, "end": v(7.43, 39.66) * mm});
            skArc(sketch, "E10.29.3", {"start": v(7.43, 39.66) * mm, "mid": v(7.29, 39.9) * mm, "end": v(7.03, 40.03) * mm});
            skArc(sketch, "E10.29.4", {"start": v(7.03, 40.03) * mm, "mid": v(6.36, 40.14) * mm, "end": v(5.68, 40.24) * mm});
            skArc(sketch, "E10.29.5", {"start": v(5.68, 40.24) * mm, "mid": v(5.4, 40.2) * mm, "end": v(5.19, 40.02) * mm});
            skArc(sketch, "E10.29.6", {"start": v(4.12, 38.16) * mm, "mid": v(4.63, 39.1) * mm, "end": v(5.19, 40.02) * mm});
            skArc(sketch, "E10.29.7", {"start": v(4.12, 38.16) * mm, "mid": v(4, 37.9) * mm, "end": v(3.95, 37.6) * mm});
            skLineSegment(sketch, "E10.29.8", {"start": v(3.72, 35.37) * mm, "end": v(3.95, 37.6) * mm});
            skArc(sketch, "E11.trimOffspring", {"start": v(3.72, 35.37) * mm, "mid": v(1.86, 35.51) * mm, "end": v(0, 35.56) * mm});
            skArc(sketch, "E12.trimOffspring", {"start": v(10.99, 33.82) * mm, "mid": v(9.2, 34.35) * mm, "end": v(7.4, 34.78) * mm});
            skArc(sketch, "E13.trimOffspring", {"start": v(17.78, 30.8) * mm, "mid": v(16.14, 31.68) * mm, "end": v(14.46, 32.49) * mm});
            skArc(sketch, "E14.trimOffspring", {"start": v(23.8, 26.43) * mm, "mid": v(22.38, 27.64) * mm, "end": v(20.9, 28.77) * mm});
            skArc(sketch, "E15.trimOffspring", {"start": v(28.77, 20.9) * mm, "mid": v(27.64, 22.38) * mm, "end": v(26.43, 23.8) * mm});
            skArc(sketch, "E16.trimOffspring", {"start": v(32.49, 14.46) * mm, "mid": v(31.68, 16.14) * mm, "end": v(30.8, 17.78) * mm});
            skArc(sketch, "E17.trimOffspring", {"start": v(34.78, 7.4) * mm, "mid": v(34.35, 9.2) * mm, "end": v(33.82, 10.99) * mm});
            skArc(sketch, "E18.trimOffspring", {"start": v(35.56, 0) * mm, "mid": v(35.51, 1.86) * mm, "end": v(35.37, 3.72) * mm});
            skArc(sketch, "E19.trimOffspring", {"start": v(34.78, -7.4) * mm, "mid": v(35.12, -5.56) * mm, "end": v(35.37, -3.72) * mm});
            skArc(sketch, "E20.trimOffspring", {"start": v(32.49, -14.46) * mm, "mid": v(33.2, -12.74) * mm, "end": v(33.82, -10.99) * mm});
            skArc(sketch, "E21.trimOffspring", {"start": v(28.77, -20.9) * mm, "mid": v(29.82, -19.37) * mm, "end": v(30.8, -17.78) * mm});
            skArc(sketch, "E22.trimOffspring", {"start": v(23.8, -26.43) * mm, "mid": v(25.14, -25.14) * mm, "end": v(26.43, -23.8) * mm});
            skArc(sketch, "E23.trimOffspring", {"start": v(17.78, -30.8) * mm, "mid": v(19.37, -29.82) * mm, "end": v(20.9, -28.77) * mm});
            skArc(sketch, "E24.trimOffspring", {"start": v(10.99, -33.82) * mm, "mid": v(12.74, -33.2) * mm, "end": v(14.46, -32.49) * mm});
            skArc(sketch, "E25.trimOffspring", {"start": v(3.72, -35.37) * mm, "mid": v(5.56, -35.12) * mm, "end": v(7.4, -34.78) * mm});
            skArc(sketch, "E26.trimOffspring", {"start": v(-3.72, -35.37) * mm, "mid": v(-1.86, -35.51) * mm, "end": v(0, -35.56) * mm});
            skArc(sketch, "E27.trimOffspring", {"start": v(-10.99, -33.82) * mm, "mid": v(-9.2, -34.35) * mm, "end": v(-7.4, -34.78) * mm});
            skArc(sketch, "E28.trimOffspring", {"start": v(-17.78, -30.8) * mm, "mid": v(-16.14, -31.68) * mm, "end": v(-14.46, -32.49) * mm});
            skArc(sketch, "E29.trimOffspring", {"start": v(-23.8, -26.43) * mm, "mid": v(-22.38, -27.64) * mm, "end": v(-20.9, -28.77) * mm});
            skArc(sketch, "E30.trimOffspring", {"start": v(-28.77, -20.9) * mm, "mid": v(-27.64, -22.38) * mm, "end": v(-26.43, -23.8) * mm});
            skArc(sketch, "E31.trimOffspring", {"start": v(-32.49, -14.46) * mm, "mid": v(-31.68, -16.14) * mm, "end": v(-30.8, -17.78) * mm});
            skArc(sketch, "E32.trimOffspring", {"start": v(-34.78, -7.4) * mm, "mid": v(-34.35, -9.2) * mm, "end": v(-33.82, -10.99) * mm});
            skArc(sketch, "E33.trimOffspring", {"start": v(-35.56, 0) * mm, "mid": v(-35.51, -1.86) * mm, "end": v(-35.37, -3.72) * mm});
            skArc(sketch, "E34.trimOffspring", {"start": v(-34.78, 7.4) * mm, "mid": v(-35.12, 5.56) * mm, "end": v(-35.37, 3.72) * mm});
            skArc(sketch, "E35.trimOffspring", {"start": v(-32.49, 14.46) * mm, "mid": v(-33.2, 12.74) * mm, "end": v(-33.82, 10.99) * mm});
            skArc(sketch, "E36.trimOffspring", {"start": v(-28.77, 20.9) * mm, "mid": v(-29.82, 19.37) * mm, "end": v(-30.8, 17.78) * mm});
            skArc(sketch, "E37.trimOffspring", {"start": v(-23.8, 26.43) * mm, "mid": v(-25.14, 25.14) * mm, "end": v(-26.43, 23.8) * mm});
            skArc(sketch, "E38.trimOffspring", {"start": v(-17.78, 30.8) * mm, "mid": v(-19.37, 29.82) * mm, "end": v(-20.9, 28.77) * mm});
            skArc(sketch, "E39.trimOffspring", {"start": v(-10.99, 33.82) * mm, "mid": v(-12.74, 33.2) * mm, "end": v(-14.46, 32.49) * mm});
            skCircle(sketch, "E40", {"center": v(0, 0) * mm, "radius": 12.7 * mm});
            skSolve(sketch);
        }
        {
            var Q0;
            Q0=makeQuery(id+"F0.imprint","IMPRINT",FACE,{"disambiguationData":[TD([[makeQuery(id+"F0.imprint","IMPRINT",EDGE,{"derivedFrom":sQuery(id+"F0.wireOp",EDGE,"E0")}),1.0]])]});
            extrude(context, id + "F1", {"entities" : qUnion([Q0]), "depth" : 114.3 * mm});
        }
        {
            var Q0;
            Q0=makeQuery(id+"F0.imprint","IMPRINT",FACE,{"disambiguationData":[TD([[makeQuery(id+"F0.imprint","IMPRINT",EDGE,{"derivedFrom":sQuery(id+"F0.wireOp",EDGE,"E40")}),1.0]])]});
            extrude(context, id + "F2", {"entities" : qUnion([Q0]), "operationType" : NewBodyOperationType.ADD, "depth" : 127 * mm});
        }
        {
            var Q0;
            Q0=sQuery(id+"F0.wireOp",VERTEX,"E0.center");
            var Q1;
            Q1=makeQuery(id+"F1.opExtrude","SWEPT_BODY",BODY,{"disambiguationData":[OSD([sQuery(id+"F0.wireOp",EDGE,"E0"),sQuery(id+"F0.wireOp",EDGE,"E1"),sQuery(id+"F0.wireOp",EDGE,"E2"),sQuery(id+"F0.wireOp",EDGE,"E3.trimOffspring"),sQuery(id+"F0.wireOp",EDGE,"E4.MirrorCS"),sQuery(id+"F0.wireOp",EDGE,"E5.MirrorCS"),sQuery(id+"F0.wireOp",EDGE,"E6.filletArc"),sQuery(id+"F0.wireOp",EDGE,"E7.filletArc"),sQuery(id+"F0.wireOp",EDGE,"E8.filletArc"),sQuery(id+"F0.wireOp",EDGE,"E9.filletArc"),sQuery(id+"F0.wireOp",EDGE,"E10.1.0"),sQuery(id+"F0.wireOp",EDGE,"E10.1.1"),sQuery(id+"F0.wireOp",EDGE,"E10.1.2"),sQuery(id+"F0.wireOp",EDGE,"E10.1.3"),sQuery(id+"F0.wireOp",EDGE,"E10.1.4"),sQuery(id+"F0.wireOp",EDGE,"E10.1.5"),sQuery(id+"F0.wireOp",EDGE,"E10.1.6"),sQuery(id+"F0.wireOp",EDGE,"E10.1.7"),sQuery(id+"F0.wireOp",EDGE,"E10.1.8"),sQuery(id+"F0.wireOp",EDGE,"E10.2.0"),sQuery(id+"F0.wireOp",EDGE,"E10.2.1"),sQuery(id+"F0.wireOp",EDGE,"E10.2.2"),sQuery(id+"F0.wireOp",EDGE,"E10.2.3"),sQuery(id+"F0.wireOp",EDGE,"E10.2.4"),sQuery(id+"F0.wireOp",EDGE,"E10.2.5"),sQuery(id+"F0.wireOp",EDGE,"E10.2.6"),sQuery(id+"F0.wireOp",EDGE,"E10.2.7"),sQuery(id+"F0.wireOp",EDGE,"E10.2.8"),sQuery(id+"F0.wireOp",EDGE,"E10.3.0"),sQuery(id+"F0.wireOp",EDGE,"E10.3.1"),sQuery(id+"F0.wireOp",EDGE,"E10.3.2"),sQuery(id+"F0.wireOp",EDGE,"E10.3.3"),sQuery(id+"F0.wireOp",EDGE,"E10.3.4"),sQuery(id+"F0.wireOp",EDGE,"E10.3.5"),sQuery(id+"F0.wireOp",EDGE,"E10.3.6"),sQuery(id+"F0.wireOp",EDGE,"E10.3.7"),sQuery(id+"F0.wireOp",EDGE,"E10.3.8"),sQuery(id+"F0.wireOp",EDGE,"E10.4.0"),sQuery(id+"F0.wireOp",EDGE,"E10.4.1"),sQuery(id+"F0.wireOp",EDGE,"E10.4.2"),sQuery(id+"F0.wireOp",EDGE,"E10.4.3"),sQuery(id+"F0.wireOp",EDGE,"E10.4.4"),sQuery(id+"F0.wireOp",EDGE,"E10.4.5"),sQuery(id+"F0.wireOp",EDGE,"E10.4.6"),sQuery(id+"F0.wireOp",EDGE,"E10.4.7"),sQuery(id+"F0.wireOp",EDGE,"E10.4.8"),sQuery(id+"F0.wireOp",EDGE,"E10.5.0"),sQuery(id+"F0.wireOp",EDGE,"E10.5.1"),sQuery(id+"F0.wireOp",EDGE,"E10.5.2"),sQuery(id+"F0.wireOp",EDGE,"E10.5.3"),sQuery(id+"F0.wireOp",EDGE,"E10.5.4"),sQuery(id+"F0.wireOp",EDGE,"E10.5.5"),sQuery(id+"F0.wireOp",EDGE,"E10.5.6"),sQuery(id+"F0.wireOp",EDGE,"E10.5.7"),sQuery(id+"F0.wireOp",EDGE,"E10.5.8"),sQuery(id+"F0.wireOp",EDGE,"E10.6.0"),sQuery(id+"F0.wireOp",EDGE,"E10.6.1"),sQuery(id+"F0.wireOp",EDGE,"E10.6.2"),sQuery(id+"F0.wireOp",EDGE,"E10.6.3"),sQuery(id+"F0.wireOp",EDGE,"E10.6.4"),sQuery(id+"F0.wireOp",EDGE,"E10.6.5"),sQuery(id+"F0.wireOp",EDGE,"E10.6.6"),sQuery(id+"F0.wireOp",EDGE,"E10.6.7"),sQuery(id+"F0.wireOp",EDGE,"E10.6.8"),sQuery(id+"F0.wireOp",EDGE,"E10.7.0"),sQuery(id+"F0.wireOp",EDGE,"E10.7.1"),sQuery(id+"F0.wireOp",EDGE,"E10.7.2"),sQuery(id+"F0.wireOp",EDGE,"E10.7.3"),sQuery(id+"F0.wireOp",EDGE,"E10.7.4"),sQuery(id+"F0.wireOp",EDGE,"E10.7.5"),sQuery(id+"F0.wireOp",EDGE,"E10.7.6"),sQuery(id+"F0.wireOp",EDGE,"E10.7.7"),sQuery(id+"F0.wireOp",EDGE,"E10.7.8"),sQuery(id+"F0.wireOp",EDGE,"E10.8.0"),sQuery(id+"F0.wireOp",EDGE,"E10.8.1"),sQuery(id+"F0.wireOp",EDGE,"E10.8.2"),sQuery(id+"F0.wireOp",EDGE,"E10.8.3"),sQuery(id+"F0.wireOp",EDGE,"E10.8.4"),sQuery(id+"F0.wireOp",EDGE,"E10.8.5"),sQuery(id+"F0.wireOp",EDGE,"E10.8.6"),sQuery(id+"F0.wireOp",EDGE,"E10.8.7"),sQuery(id+"F0.wireOp",EDGE,"E10.8.8"),sQuery(id+"F0.wireOp",EDGE,"E10.9.0"),sQuery(id+"F0.wireOp",EDGE,"E10.9.1"),sQuery(id+"F0.wireOp",EDGE,"E10.9.2"),sQuery(id+"F0.wireOp",EDGE,"E10.9.3"),sQuery(id+"F0.wireOp",EDGE,"E10.9.4"),sQuery(id+"F0.wireOp",EDGE,"E10.9.5"),sQuery(id+"F0.wireOp",EDGE,"E10.9.6"),sQuery(id+"F0.wireOp",EDGE,"E10.9.7"),sQuery(id+"F0.wireOp",EDGE,"E10.9.8"),sQuery(id+"F0.wireOp",EDGE,"E10.10.0"),sQuery(id+"F0.wireOp",EDGE,"E10.10.1"),sQuery(id+"F0.wireOp",EDGE,"E10.10.2"),sQuery(id+"F0.wireOp",EDGE,"E10.10.3"),sQuery(id+"F0.wireOp",EDGE,"E10.10.4"),sQuery(id+"F0.wireOp",EDGE,"E10.10.5"),sQuery(id+"F0.wireOp",EDGE,"E10.10.6"),sQuery(id+"F0.wireOp",EDGE,"E10.10.7"),sQuery(id+"F0.wireOp",EDGE,"E10.10.8"),sQuery(id+"F0.wireOp",EDGE,"E10.11.0"),sQuery(id+"F0.wireOp",EDGE,"E10.11.1"),sQuery(id+"F0.wireOp",EDGE,"E10.11.2"),sQuery(id+"F0.wireOp",EDGE,"E10.11.3"),sQuery(id+"F0.wireOp",EDGE,"E10.11.4"),sQuery(id+"F0.wireOp",EDGE,"E10.11.5"),sQuery(id+"F0.wireOp",EDGE,"E10.11.6"),sQuery(id+"F0.wireOp",EDGE,"E10.11.7"),sQuery(id+"F0.wireOp",EDGE,"E10.11.8"),sQuery(id+"F0.wireOp",EDGE,"E10.12.0"),sQuery(id+"F0.wireOp",EDGE,"E10.12.1"),sQuery(id+"F0.wireOp",EDGE,"E10.12.2"),sQuery(id+"F0.wireOp",EDGE,"E10.12.3"),sQuery(id+"F0.wireOp",EDGE,"E10.12.4"),sQuery(id+"F0.wireOp",EDGE,"E10.12.5"),sQuery(id+"F0.wireOp",EDGE,"E10.12.6"),sQuery(id+"F0.wireOp",EDGE,"E10.12.7"),sQuery(id+"F0.wireOp",EDGE,"E10.12.8"),sQuery(id+"F0.wireOp",EDGE,"E10.13.0"),sQuery(id+"F0.wireOp",EDGE,"E10.13.1"),sQuery(id+"F0.wireOp",EDGE,"E10.13.2"),sQuery(id+"F0.wireOp",EDGE,"E10.13.3"),sQuery(id+"F0.wireOp",EDGE,"E10.13.4"),sQuery(id+"F0.wireOp",EDGE,"E10.13.5"),sQuery(id+"F0.wireOp",EDGE,"E10.13.6"),sQuery(id+"F0.wireOp",EDGE,"E10.13.7"),sQuery(id+"F0.wireOp",EDGE,"E10.13.8"),sQuery(id+"F0.wireOp",EDGE,"E10.14.0"),sQuery(id+"F0.wireOp",EDGE,"E10.14.1"),sQuery(id+"F0.wireOp",EDGE,"E10.14.2"),sQuery(id+"F0.wireOp",EDGE,"E10.14.3"),sQuery(id+"F0.wireOp",EDGE,"E10.14.4"),sQuery(id+"F0.wireOp",EDGE,"E10.14.5"),sQuery(id+"F0.wireOp",EDGE,"E10.14.6"),sQuery(id+"F0.wireOp",EDGE,"E10.14.7"),sQuery(id+"F0.wireOp",EDGE,"E10.14.8"),sQuery(id+"F0.wireOp",EDGE,"E10.15.0"),sQuery(id+"F0.wireOp",EDGE,"E10.15.1"),sQuery(id+"F0.wireOp",EDGE,"E10.15.2"),sQuery(id+"F0.wireOp",EDGE,"E10.15.3"),sQuery(id+"F0.wireOp",EDGE,"E10.15.4"),sQuery(id+"F0.wireOp",EDGE,"E10.15.5"),sQuery(id+"F0.wireOp",EDGE,"E10.15.6"),sQuery(id+"F0.wireOp",EDGE,"E10.15.7"),sQuery(id+"F0.wireOp",EDGE,"E10.15.8"),sQuery(id+"F0.wireOp",EDGE,"E10.16.0"),sQuery(id+"F0.wireOp",EDGE,"E10.16.1"),sQuery(id+"F0.wireOp",EDGE,"E10.16.2"),sQuery(id+"F0.wireOp",EDGE,"E10.16.3"),sQuery(id+"F0.wireOp",EDGE,"E10.16.4"),sQuery(id+"F0.wireOp",EDGE,"E10.16.5"),sQuery(id+"F0.wireOp",EDGE,"E10.16.6"),sQuery(id+"F0.wireOp",EDGE,"E10.16.7"),sQuery(id+"F0.wireOp",EDGE,"E10.16.8"),sQuery(id+"F0.wireOp",EDGE,"E10.17.0"),sQuery(id+"F0.wireOp",EDGE,"E10.17.1"),sQuery(id+"F0.wireOp",EDGE,"E10.17.2"),sQuery(id+"F0.wireOp",EDGE,"E10.17.3"),sQuery(id+"F0.wireOp",EDGE,"E10.17.4"),sQuery(id+"F0.wireOp",EDGE,"E10.17.5"),sQuery(id+"F0.wireOp",EDGE,"E10.17.6"),sQuery(id+"F0.wireOp",EDGE,"E10.17.7"),sQuery(id+"F0.wireOp",EDGE,"E10.17.8"),sQuery(id+"F0.wireOp",EDGE,"E10.18.0"),sQuery(id+"F0.wireOp",EDGE,"E10.18.1"),sQuery(id+"F0.wireOp",EDGE,"E10.18.2"),sQuery(id+"F0.wireOp",EDGE,"E10.18.3"),sQuery(id+"F0.wireOp",EDGE,"E10.18.4"),sQuery(id+"F0.wireOp",EDGE,"E10.18.5"),sQuery(id+"F0.wireOp",EDGE,"E10.18.6"),sQuery(id+"F0.wireOp",EDGE,"E10.18.7"),sQuery(id+"F0.wireOp",EDGE,"E10.18.8"),sQuery(id+"F0.wireOp",EDGE,"E10.19.0"),sQuery(id+"F0.wireOp",EDGE,"E10.19.1"),sQuery(id+"F0.wireOp",EDGE,"E10.19.2"),sQuery(id+"F0.wireOp",EDGE,"E10.19.3"),sQuery(id+"F0.wireOp",EDGE,"E10.19.4"),sQuery(id+"F0.wireOp",EDGE,"E10.19.5"),sQuery(id+"F0.wireOp",EDGE,"E10.19.6"),sQuery(id+"F0.wireOp",EDGE,"E10.19.7"),sQuery(id+"F0.wireOp",EDGE,"E10.19.8"),sQuery(id+"F0.wireOp",EDGE,"E10.20.0"),sQuery(id+"F0.wireOp",EDGE,"E10.20.1"),sQuery(id+"F0.wireOp",EDGE,"E10.20.2"),sQuery(id+"F0.wireOp",EDGE,"E10.20.3"),sQuery(id+"F0.wireOp",EDGE,"E10.20.4"),sQuery(id+"F0.wireOp",EDGE,"E10.20.5"),sQuery(id+"F0.wireOp",EDGE,"E10.20.6"),sQuery(id+"F0.wireOp",EDGE,"E10.20.7"),sQuery(id+"F0.wireOp",EDGE,"E10.20.8"),sQuery(id+"F0.wireOp",EDGE,"E10.21.0"),sQuery(id+"F0.wireOp",EDGE,"E10.21.1"),sQuery(id+"F0.wireOp",EDGE,"E10.21.2"),sQuery(id+"F0.wireOp",EDGE,"E10.21.3"),sQuery(id+"F0.wireOp",EDGE,"E10.21.4"),sQuery(id+"F0.wireOp",EDGE,"E10.21.5"),sQuery(id+"F0.wireOp",EDGE,"E10.21.6"),sQuery(id+"F0.wireOp",EDGE,"E10.21.7"),sQuery(id+"F0.wireOp",EDGE,"E10.21.8"),sQuery(id+"F0.wireOp",EDGE,"E10.22.0"),sQuery(id+"F0.wireOp",EDGE,"E10.22.1"),sQuery(id+"F0.wireOp",EDGE,"E10.22.2"),sQuery(id+"F0.wireOp",EDGE,"E10.22.3"),sQuery(id+"F0.wireOp",EDGE,"E10.22.4"),sQuery(id+"F0.wireOp",EDGE,"E10.22.5"),sQuery(id+"F0.wireOp",EDGE,"E10.22.6"),sQuery(id+"F0.wireOp",EDGE,"E10.22.7"),sQuery(id+"F0.wireOp",EDGE,"E10.22.8"),sQuery(id+"F0.wireOp",EDGE,"E10.23.0"),sQuery(id+"F0.wireOp",EDGE,"E10.23.1"),sQuery(id+"F0.wireOp",EDGE,"E10.23.2"),sQuery(id+"F0.wireOp",EDGE,"E10.23.3"),sQuery(id+"F0.wireOp",EDGE,"E10.23.4"),sQuery(id+"F0.wireOp",EDGE,"E10.23.5"),sQuery(id+"F0.wireOp",EDGE,"E10.23.6"),sQuery(id+"F0.wireOp",EDGE,"E10.23.7"),sQuery(id+"F0.wireOp",EDGE,"E10.23.8"),sQuery(id+"F0.wireOp",EDGE,"E10.24.0"),sQuery(id+"F0.wireOp",EDGE,"E10.24.1"),sQuery(id+"F0.wireOp",EDGE,"E10.24.2"),sQuery(id+"F0.wireOp",EDGE,"E10.24.3"),sQuery(id+"F0.wireOp",EDGE,"E10.24.4"),sQuery(id+"F0.wireOp",EDGE,"E10.24.5"),sQuery(id+"F0.wireOp",EDGE,"E10.24.6"),sQuery(id+"F0.wireOp",EDGE,"E10.24.7"),sQuery(id+"F0.wireOp",EDGE,"E10.24.8"),sQuery(id+"F0.wireOp",EDGE,"E10.25.0"),sQuery(id+"F0.wireOp",EDGE,"E10.25.1"),sQuery(id+"F0.wireOp",EDGE,"E10.25.2"),sQuery(id+"F0.wireOp",EDGE,"E10.25.3"),sQuery(id+"F0.wireOp",EDGE,"E10.25.4"),sQuery(id+"F0.wireOp",EDGE,"E10.25.5"),sQuery(id+"F0.wireOp",EDGE,"E10.25.6"),sQuery(id+"F0.wireOp",EDGE,"E10.25.7"),sQuery(id+"F0.wireOp",EDGE,"E10.25.8"),sQuery(id+"F0.wireOp",EDGE,"E10.26.0"),sQuery(id+"F0.wireOp",EDGE,"E10.26.1"),sQuery(id+"F0.wireOp",EDGE,"E10.26.2"),sQuery(id+"F0.wireOp",EDGE,"E10.26.3"),sQuery(id+"F0.wireOp",EDGE,"E10.26.4"),sQuery(id+"F0.wireOp",EDGE,"E10.26.5"),sQuery(id+"F0.wireOp",EDGE,"E10.26.6"),sQuery(id+"F0.wireOp",EDGE,"E10.26.7"),sQuery(id+"F0.wireOp",EDGE,"E10.26.8"),sQuery(id+"F0.wireOp",EDGE,"E10.27.0"),sQuery(id+"F0.wireOp",EDGE,"E10.27.1"),sQuery(id+"F0.wireOp",EDGE,"E10.27.2"),sQuery(id+"F0.wireOp",EDGE,"E10.27.3"),sQuery(id+"F0.wireOp",EDGE,"E10.27.4"),sQuery(id+"F0.wireOp",EDGE,"E10.27.5"),sQuery(id+"F0.wireOp",EDGE,"E10.27.6"),sQuery(id+"F0.wireOp",EDGE,"E10.27.7"),sQuery(id+"F0.wireOp",EDGE,"E10.27.8"),sQuery(id+"F0.wireOp",EDGE,"E10.28.0"),sQuery(id+"F0.wireOp",EDGE,"E10.28.1"),sQuery(id+"F0.wireOp",EDGE,"E10.28.2"),sQuery(id+"F0.wireOp",EDGE,"E10.28.3"),sQuery(id+"F0.wireOp",EDGE,"E10.28.4"),sQuery(id+"F0.wireOp",EDGE,"E10.28.5"),sQuery(id+"F0.wireOp",EDGE,"E10.28.6"),sQuery(id+"F0.wireOp",EDGE,"E10.28.7"),sQuery(id+"F0.wireOp",EDGE,"E10.28.8"),sQuery(id+"F0.wireOp",EDGE,"E10.29.0"),sQuery(id+"F0.wireOp",EDGE,"E10.29.1"),sQuery(id+"F0.wireOp",EDGE,"E10.29.2"),sQuery(id+"F0.wireOp",EDGE,"E10.29.3"),sQuery(id+"F0.wireOp",EDGE,"E10.29.4"),sQuery(id+"F0.wireOp",EDGE,"E10.29.5"),sQuery(id+"F0.wireOp",EDGE,"E10.29.6"),sQuery(id+"F0.wireOp",EDGE,"E10.29.7"),sQuery(id+"F0.wireOp",EDGE,"E10.29.8"),sQuery(id+"F0.wireOp",EDGE,"E11.trimOffspring"),sQuery(id+"F0.wireOp",EDGE,"E12.trimOffspring"),sQuery(id+"F0.wireOp",EDGE,"E13.trimOffspring"),sQuery(id+"F0.wireOp",EDGE,"E14.trimOffspring"),sQuery(id+"F0.wireOp",EDGE,"E15.trimOffspring"),sQuery(id+"F0.wireOp",EDGE,"E16.trimOffspring"),sQuery(id+"F0.wireOp",EDGE,"E17.trimOffspring"),sQuery(id+"F0.wireOp",EDGE,"E18.trimOffspring"),sQuery(id+"F0.wireOp",EDGE,"E19.trimOffspring"),sQuery(id+"F0.wireOp",EDGE,"E20.trimOffspring"),sQuery(id+"F0.wireOp",EDGE,"E21.trimOffspring"),sQuery(id+"F0.wireOp",EDGE,"E22.trimOffspring"),sQuery(id+"F0.wireOp",EDGE,"E23.trimOffspring"),sQuery(id+"F0.wireOp",EDGE,"E24.trimOffspring"),sQuery(id+"F0.wireOp",EDGE,"E25.trimOffspring"),sQuery(id+"F0.wireOp",EDGE,"E26.trimOffspring"),sQuery(id+"F0.wireOp",EDGE,"E27.trimOffspring"),sQuery(id+"F0.wireOp",EDGE,"E28.trimOffspring"),sQuery(id+"F0.wireOp",EDGE,"E29.trimOffspring"),sQuery(id+"F0.wireOp",EDGE,"E30.trimOffspring"),sQuery(id+"F0.wireOp",EDGE,"E31.trimOffspring"),sQuery(id+"F0.wireOp",EDGE,"E32.trimOffspring"),sQuery(id+"F0.wireOp",EDGE,"E33.trimOffspring"),sQuery(id+"F0.wireOp",EDGE,"E34.trimOffspring"),sQuery(id+"F0.wireOp",EDGE,"E35.trimOffspring"),sQuery(id+"F0.wireOp",EDGE,"E36.trimOffspring"),sQuery(id+"F0.wireOp",EDGE,"E37.trimOffspring"),sQuery(id+"F0.wireOp",EDGE,"E38.trimOffspring"),sQuery(id+"F0.wireOp",EDGE,"E39.trimOffspring"),sQuery(id+"F0.wireOp",EDGE,"E40")])]});
            hole(context, id + "F3", {"style" : HoleStyle.SIMPLE, "endStyle" : HoleEndStyle.BLIND, "oppositeDirection" : true, "holeDiameter" : 12.7 * mm, "holeDepth" : 127 * mm, "tappedDepth" : 12.7 * mm, "tapClearance" : 3, "startFromSketch" : true, "locations" : qUnion([Q0]), "scope" : qUnion([Q1])});
        }
    });
